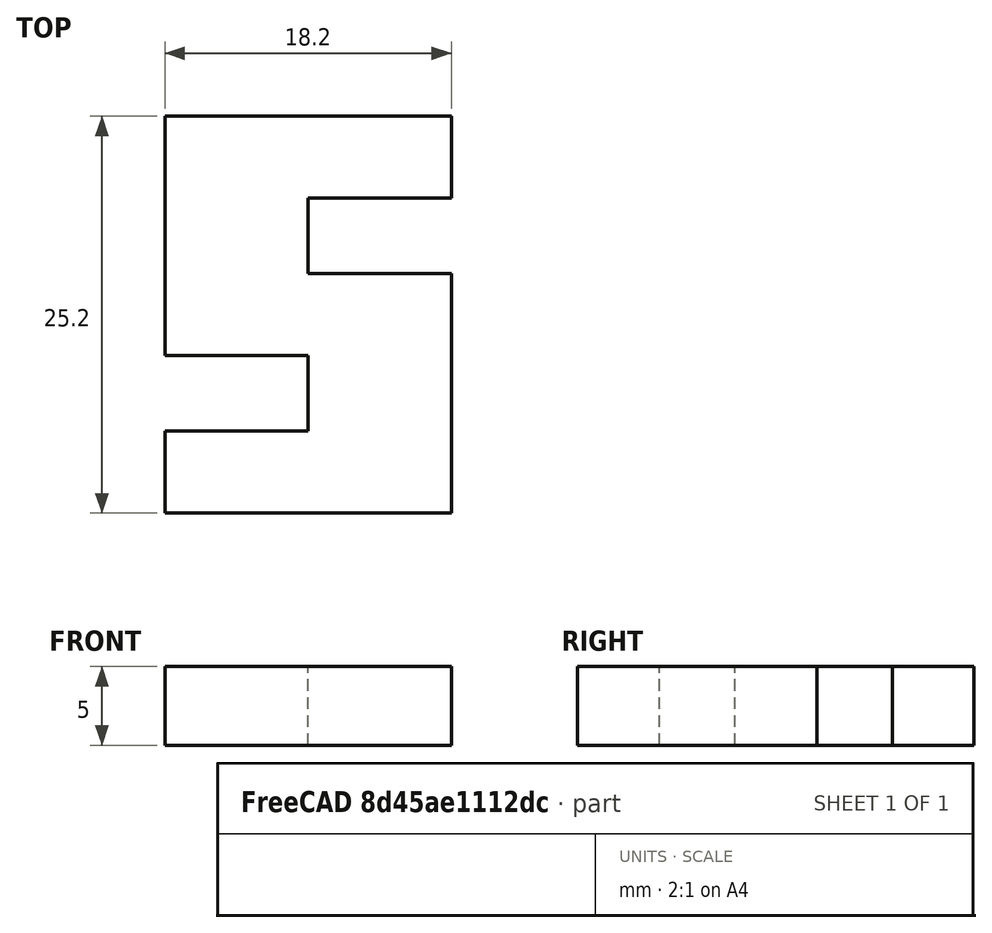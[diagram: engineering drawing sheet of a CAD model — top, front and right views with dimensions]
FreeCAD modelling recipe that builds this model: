
FCSTD DOCUMENT  (FreeCAD 0.16R6707 (Git))
Label: AssemblerMK2
License: All rights reserved
LicenseURL: http://en.wikipedia.org/wiki/All_rights_reserved
objects: Sketcher::SketchObject×1, PartDesign::Pad×1
note: 3 computed .brp shape members not serialized (recipe doc carries the construction recipe); baked Part::Feature solids carry a one-line shape summary decoded from their .brp

FEATURE [Sketcher::SketchObject] Sketch
  sketch-geometry (12):
    g0: LineSegment StartX=-9.1 StartY=12.6 StartZ=0 EndX=9.1 EndY=12.6 EndZ=0
    g1: LineSegment StartX=9.1 StartY=12.6 StartZ=0 EndX=9.1 EndY=7.4 EndZ=0
    g2: LineSegment StartX=9.1 StartY=7.4 StartZ=0 EndX=0 EndY=7.4 EndZ=0
    g3: LineSegment StartX=0 StartY=7.4 StartZ=0 EndX=0 EndY=2.6 EndZ=0
    g4: LineSegment StartX=0 StartY=2.6 StartZ=0 EndX=9.1 EndY=2.6 EndZ=0
    g5: LineSegment StartX=9.1 StartY=2.6 StartZ=0 EndX=9.1 EndY=-12.6 EndZ=0
    g6: LineSegment StartX=9.1 StartY=-12.6 StartZ=0 EndX=-9.1 EndY=-12.6 EndZ=0
    g7: LineSegment StartX=-9.1 StartY=-12.6 StartZ=0 EndX=-9.1 EndY=-7.4 EndZ=0
    g8: LineSegment StartX=-9.1 StartY=-7.4 StartZ=0 EndX=0 EndY=-7.4 EndZ=0
    g9: LineSegment StartX=0 StartY=-7.4 StartZ=0 EndX=0 EndY=-2.6 EndZ=0
    g10: LineSegment StartX=0 StartY=-2.6 StartZ=0 EndX=-9.1 EndY=-2.6 EndZ=0
    g11: LineSegment StartX=-9.1 StartY=-2.6 StartZ=0 EndX=-9.1 EndY=12.6 EndZ=0
  constraints (35):
    c: Horizontal(g0)
    c: Coincident(g0,g1)
    c: Vertical(g1)
    c: Coincident(g1,g2)
    c: PointOnObject(g2,g-2)
    c: Horizontal(g2)
    c: Coincident(g2,g3)
    c: Vertical(g3)
    c: Coincident(g3,g4)
    c: Horizontal(g4)
    c: Coincident(g4,g5)
    c: Vertical(g5)
    c: Coincident(g5,g6)
    c: Horizontal(g6)
    c: Coincident(g6,g7)
    c: Vertical(g7)
    c: Coincident(g7,g8)
    c: PointOnObject(g8,g-2)
    c: Horizontal(g8)
    c: Coincident(g8,g9)
    c: Vertical(g9)
    c: Coincident(g9,g10)
    c: Horizontal(g10)
    c: Coincident(g10,g11)
    c: Coincident(g11,g0)
    c: Vertical(g11)
    c: Symmetric(g0,g6,g-1)
    c: Symmetric(g6,g5,g-2)
    c: Symmetric(g0,g0,g-2)
    c: Equal(g3,g9)
    c: Symmetric(g3,g9,g-1)
    c: DistanceY(g9,g3) = 5.2
    c: DistanceY(g9,g9) = 4.8
    c: DistanceY(g7,g7) = 5.2
    c: DistanceX(g0,g0) = 18.2
FEATURE [PartDesign::Pad] Pad
  Length = 5
  Length2 = 100
  Sketch = -> Sketch
  Type = 0
